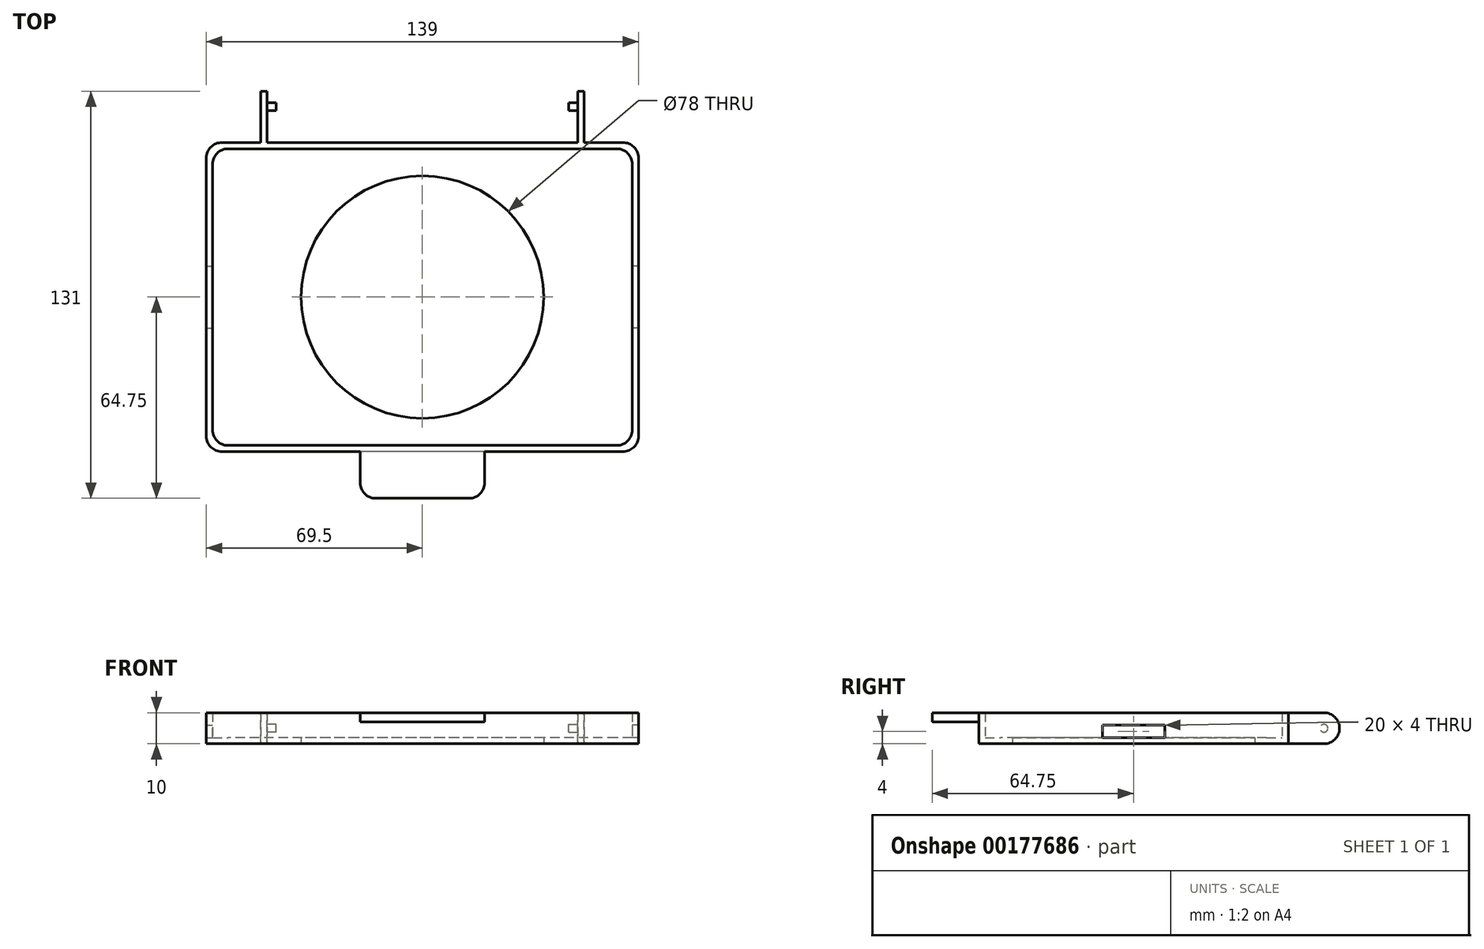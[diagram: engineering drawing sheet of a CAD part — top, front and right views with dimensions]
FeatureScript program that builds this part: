
annotation { "Feature Type Name" : "Feature", "Feature Type Description" : "" }
export const myFeature = defineFeature(function(context is Context, id is Id, definition is map)
    precondition{}
    {
        {
            var Q0;
            Q0=qCreatedBy(makeId("Top.planeOp"),FACE);
            var sketch = newSketch(context, id + "F0", { "sketchPlane" : qUnion([Q0])});
            skLineSegment(sketch, "E0.bottom", {"start": v(62.5, 47.75) * mm, "end": v(-62.5, 47.75) * mm});
            skLineSegment(sketch, "E0.top", {"start": v(62.5, -47.75) * mm, "end": v(-62.5, -47.75) * mm});
            skLineSegment(sketch, "E0.left", {"start": v(67.5, 42.75) * mm, "end": v(67.5, -42.75) * mm});
            skLineSegment(sketch, "E0.right", {"start": v(-67.5, 42.75) * mm, "end": v(-67.5, -42.75) * mm});
            skPoint(sketch, "E0.middle", {"position": v(0, 0) * mm});
            skLineSegment(sketch, "E1.0", {"start": v(64.5, 49.75) * mm, "end": v(-64.5, 49.75) * mm});
            skLineSegment(sketch, "E1.1", {"start": v(69.5, 44.75) * mm, "end": v(69.5, -44.75) * mm});
            skLineSegment(sketch, "E1.2", {"start": v(64.5, -49.75) * mm, "end": v(-64.5, -49.75) * mm});
            skLineSegment(sketch, "E1.3", {"start": v(-69.5, 44.75) * mm, "end": v(-69.5, -44.75) * mm});
            skPoint(sketch, "E2.visualSharp", {"position": v(-69.5, -49.75) * mm});
            skArc(sketch, "E2.filletArc", {"start": v(-69.5, -44.75) * mm, "mid": v(-68.04, -48.29) * mm, "end": v(-64.5, -49.75) * mm});
            skPoint(sketch, "E3.visualSharp", {"position": v(-69.5, 49.75) * mm});
            skArc(sketch, "E3.filletArc", {"start": v(-64.5, 49.75) * mm, "mid": v(-68.04, 48.29) * mm, "end": v(-69.5, 44.75) * mm});
            skPoint(sketch, "E4.visualSharp", {"position": v(69.5, -49.75) * mm});
            skArc(sketch, "E4.filletArc", {"start": v(64.5, -49.75) * mm, "mid": v(68.04, -48.29) * mm, "end": v(69.5, -44.75) * mm});
            skPoint(sketch, "E5.visualSharp", {"position": v(69.5, 49.75) * mm});
            skArc(sketch, "E5.filletArc", {"start": v(69.5, 44.75) * mm, "mid": v(68.04, 48.29) * mm, "end": v(64.5, 49.75) * mm});
            skPoint(sketch, "E6.visualSharp", {"position": v(67.5, 47.75) * mm});
            skArc(sketch, "E6.filletArc", {"start": v(67.5, 42.75) * mm, "mid": v(66.04, 46.29) * mm, "end": v(62.5, 47.75) * mm});
            skPoint(sketch, "E7.visualSharp", {"position": v(67.5, -47.75) * mm});
            skArc(sketch, "E7.filletArc", {"start": v(62.5, -47.75) * mm, "mid": v(66.04, -46.29) * mm, "end": v(67.5, -42.75) * mm});
            skPoint(sketch, "E8.visualSharp", {"position": v(-67.5, 47.75) * mm});
            skArc(sketch, "E8.filletArc", {"start": v(-62.5, 47.75) * mm, "mid": v(-66.04, 46.29) * mm, "end": v(-67.5, 42.75) * mm});
            skPoint(sketch, "E9.visualSharp", {"position": v(-67.5, -47.75) * mm});
            skArc(sketch, "E9.filletArc", {"start": v(-67.5, -42.75) * mm, "mid": v(-66.04, -46.29) * mm, "end": v(-62.5, -47.75) * mm});
            skCircle(sketch, "E10", {"center": v(0, 0) * mm, "radius": 39 * mm});
            skSolve(sketch);
        }
        {
            var Q0;
            Q0=makeQuery(id+"F0.imprint","IMPRINT",FACE,{"disambiguationData":[TD([[makeQuery(id+"F0.imprint","IMPRINT",EDGE,{"derivedFrom":sQuery(id+"F0.wireOp",EDGE,"E0.bottom")}),-1.0]])]});
            extrude(context, id + "F1", {"entities" : qUnion([Q0]), "depth" : 10 * mm});
        }
        {
            var Q0;
            Q0=makeQuery(id+"F0.imprint","IMPRINT",FACE,{"disambiguationData":[TD([[makeQuery(id+"F0.imprint","IMPRINT",EDGE,{"derivedFrom":sQuery(id+"F0.wireOp",EDGE,"E0.bottom")}),1.0]])]});
            extrude(context, id + "F2", {"entities" : qUnion([Q0]), "operationType" : NewBodyOperationType.ADD, "depth" : 2 * mm});
        }
        {
            var Q0;
            Q0=makeQuery(id+"F1.opExtrude","CAP_FACE",FACE,{"disambiguationData":[OSD([sQuery(id+"F0.wireOp",EDGE,"E0.bottom"),sQuery(id+"F0.wireOp",EDGE,"E0.top"),sQuery(id+"F0.wireOp",EDGE,"E0.left"),sQuery(id+"F0.wireOp",EDGE,"E0.right"),sQuery(id+"F0.wireOp",EDGE,"E1.0"),sQuery(id+"F0.wireOp",EDGE,"E1.1"),sQuery(id+"F0.wireOp",EDGE,"E1.2"),sQuery(id+"F0.wireOp",EDGE,"E1.3")])],"isStart":false});
            var sketch = newSketch(context, id + "F3", { "sketchPlane" : qUnion([Q0])});
            skLineSegment(sketch, "E11.bottom", {"start": v(-20, -49.75) * mm, "end": v(20, -49.75) * mm});
            skLineSegment(sketch, "E11.top", {"start": v(-15, -64.75) * mm, "end": v(15, -64.75) * mm});
            skLineSegment(sketch, "E11.left", {"start": v(-20, -49.75) * mm, "end": v(-20, -59.75) * mm});
            skLineSegment(sketch, "E11.right", {"start": v(20, -49.75) * mm, "end": v(20, -59.75) * mm});
            skPoint(sketch, "E12", {"position": v(0, -49.75) * mm});
            skPoint(sketch, "E13.visualSharp", {"position": v(-20, -64.75) * mm});
            skArc(sketch, "E13.filletArc", {"start": v(-20, -59.75) * mm, "mid": v(-18.54, -63.29) * mm, "end": v(-15, -64.75) * mm});
            skPoint(sketch, "E14.visualSharp", {"position": v(20, -64.75) * mm});
            skArc(sketch, "E14.filletArc", {"start": v(15, -64.75) * mm, "mid": v(18.54, -63.29) * mm, "end": v(20, -59.75) * mm});
            skSolve(sketch);
        }
        {
            var Q0;
            Q0=makeQuery(id+"F3.imprint","IMPRINT",FACE,{"disambiguationData":[TD([[makeQuery(id+"F3.imprint","IMPRINT",EDGE,{"derivedFrom":sQuery(id+"F3.wireOp",EDGE,"E11.bottom")}),1.0]])]});
            extrude(context, id + "F4", {"entities" : qUnion([Q0]), "operationType" : NewBodyOperationType.ADD, "oppositeDirection" : true, "depth" : 3 * mm});
        }
        {
            var Q0;
            Q0=makeQuery(id+"F1.opExtrude","SWEPT_FACE",FACE,{"disambiguationData":[OSD([sQuery(id+"F0.wireOp",EDGE,"E0.right")])]});
            var sketch = newSketch(context, id + "F5", { "sketchPlane" : qUnion([Q0])});
            skLineSegment(sketch, "E15.bottom", {"start": v(-10, 2) * mm, "end": v(10, 2) * mm});
            skLineSegment(sketch, "E15.top", {"start": v(-10, 6) * mm, "end": v(10, 6) * mm});
            skLineSegment(sketch, "E15.left", {"start": v(-10, 2) * mm, "end": v(-10, 6) * mm});
            skLineSegment(sketch, "E15.right", {"start": v(10, 2) * mm, "end": v(10, 6) * mm});
            skPoint(sketch, "E16", {"position": v(0, 2) * mm});
            skSolve(sketch);
        }
        {
            var Q0;
            Q0=makeQuery(id+"F5.imprint","IMPRINT",FACE,{"disambiguationData":[TD([[makeQuery(id+"F5.imprint","IMPRINT",EDGE,{"derivedFrom":sQuery(id+"F5.wireOp",EDGE,"E15.bottom")}),-1.0]])]});
            extrude(context, id + "F6", {"entities" : qUnion([Q0]), "operationType" : NewBodyOperationType.REMOVE, "endBound" : BoundingType.UP_TO_NEXT, "oppositeDirection" : true, "depth" : 25 * mm});
        }
        {
            var Q0;
            Q0=makeQuery(id+"F1.opExtrude","SWEPT_FACE",FACE,{"disambiguationData":[OSD([sQuery(id+"F0.wireOp",EDGE,"E0.left")])]});
            var sketch = newSketch(context, id + "F7", { "sketchPlane" : qUnion([Q0])});
            skLineSegment(sketch, "E17.0", {"start": v(10, 6) * mm, "end": v(10, 2) * mm});
            skLineSegment(sketch, "E18.0", {"start": v(10, 2) * mm, "end": v(-10, 2) * mm});
            skLineSegment(sketch, "E19.0", {"start": v(-10, 6) * mm, "end": v(10, 6) * mm});
            skLineSegment(sketch, "E20.0", {"start": v(-10, 6) * mm, "end": v(-10, 2) * mm});
            skSolve(sketch);
        }
        {
            var Q0;
            Q0=makeQuery(id+"F7.imprint","IMPRINT",FACE,{"disambiguationData":[TD([[makeQuery(id+"F7.imprint","IMPRINT",EDGE,{"derivedFrom":sQuery(id+"F7.wireOp",EDGE,"E17.0")}),-1.0]])]});
            extrude(context, id + "F8", {"entities" : qUnion([Q0]), "operationType" : NewBodyOperationType.REMOVE, "endBound" : BoundingType.UP_TO_NEXT, "oppositeDirection" : true, "depth" : 25 * mm});
        }
        {
            var Q0;
            Q0=makeQuery(id+"F1.opExtrude","SWEPT_FACE",FACE,{"disambiguationData":[OSD([sQuery(id+"F0.wireOp",EDGE,"E1.0")])]});
            var sketch = newSketch(context, id + "F9", { "sketchPlane" : qUnion([Q0])});
            skLineSegment(sketch, "E21.bottom", {"start": v(52, 0) * mm, "end": v(50, 0) * mm});
            skLineSegment(sketch, "E21.top", {"start": v(52, 10) * mm, "end": v(50, 10) * mm});
            skLineSegment(sketch, "E21.left", {"start": v(52, 0) * mm, "end": v(52, 10) * mm});
            skLineSegment(sketch, "E21.right", {"start": v(50, 0) * mm, "end": v(50, 10) * mm});
            skSolve(sketch);
        }
        {
            var Q0;
            Q0=makeQuery(id+"F9.imprint","IMPRINT",FACE,{"disambiguationData":[TD([[makeQuery(id+"F9.imprint","IMPRINT",EDGE,{"derivedFrom":sQuery(id+"F9.wireOp",EDGE,"E21.bottom")}),1.0]])]});
            var Q1;
            {var subQ0=sQuery(id+"F9.wireOp",EDGE,"c59233ef-eaf8-4a60-9904-21551acb0b020.MirrorCS");Q1=makeQuery(id+"F9.imprint","IMPRINT",FACE,{"disambiguationData":[TD([[makeQuery(id+"F9.imprint","IMPRINT",EDGE,{"derivedFrom":subQ0}),1.0]])]});}
            extrude(context, id + "F10", {"entities" : qUnion([Q0, Q1]), "operationType" : NewBodyOperationType.ADD, "depth" : 11.5 * mm});
        }
        {
            var Q0;
            Q0=makeQuery(id+"F10.opExtrude","SWEPT_FACE",FACE,{"disambiguationData":[OSD([sQuery(id+"F9.wireOp",EDGE,"E21.left")])]});
            var sketch = newSketch(context, id + "F11", { "sketchPlane" : qUnion([Q0])});
            skPoint(sketch, "E22", {"position": v(-61.25, 5) * mm});
            skCircle(sketch, "E23", {"center": v(-61.25, 5) * mm, "radius": 5 * mm});
            skSolve(sketch);
        }
        {
            var Q0;
            {var subQ1=sQuery(id+"F9.wireOp",EDGE,"E21.left");var subQ2=makeQuery(id+"F10.opExtrude","CAP_EDGE",EDGE,{"disambiguationData":[OSD([subQ1])],"isStart":false});Q0=makeQuery(id+"F11.imprint","IMPRINT",FACE,{"disambiguationData":[TD([[makeQuery(id+"F11.imprint","IMPRINT",EDGE,{"derivedFrom":subQ2}),1.0]])]});}
            extrude(context, id + "F12", {"entities" : qUnion([Q0]), "operationType" : NewBodyOperationType.ADD, "oppositeDirection" : true, "depth" : 2 * mm});
        }
        {
            var Q0;
            Q0=makeQuery(id+"F12.boolean.opBoolean","MERGE",FACE,{"derivedFrom":[makeQuery(id+"F10.opExtrude","SWEPT_FACE",FACE,{"disambiguationData":[OSD([sQuery(id+"F9.wireOp",EDGE,"E21.right")])]}),makeQuery(id+"F12.opExtrude","CAP_FACE",FACE,{"disambiguationData":[OSD([sQuery(id+"F9.wireOp",EDGE,"E21.left"),sQuery(id+"F11.wireOp",EDGE,"E23")])],"isStart":false})]});
            var sketch = newSketch(context, id + "F13", { "sketchPlane" : qUnion([Q0])});
            skCircle(sketch, "E24", {"center": v(61.25, 5) * mm, "radius": 1.25 * mm});
            skSolve(sketch);
        }
        {
            var Q0;
            Q0 = qSketchRegion(id + "F13", true);
            extrude(context, id + "F14", {"entities" : qUnion([Q0]), "operationType" : NewBodyOperationType.ADD, "depth" : 3 * mm});
        }
        {
            var Q0;
            Q0=qCreatedBy(makeId("Right.planeOp"),FACE);
            cPlane(context, id + "F15", {"entities" : qUnion([Q0]), "cplaneType" : CPlaneType.OFFSET, "offset" : 52 * mm, "width" : 150 * mm, "height" : 150 * mm});
        }
        {
            var Q0;
            Q0=qCreatedBy(id+"F15.planeOp",FACE);
            var sketch = newSketch(context, id + "F16", { "sketchPlane" : qUnion([Q0])});
            skLineSegment(sketch, "E25.0.0", {"start": v(49.75, 10) * mm, "end": v(49.75, 0) * mm});
            skLineSegment(sketch, "E25.0.1", {"start": v(49.75, 0) * mm, "end": v(61.25, 0) * mm});
            skArc(sketch, "E25.0.2", {"start": v(61.25, 0) * mm, "mid": v(66.25, 5) * mm, "end": v(61.25, 10) * mm});
            skLineSegment(sketch, "E25.0.3", {"start": v(61.25, 10) * mm, "end": v(49.75, 10) * mm});
            skCircle(sketch, "E26.0", {"center": v(61.25, 5) * mm, "radius": 1.25 * mm});
            skSolve(sketch);
        }
        {
            var Q0;
            Q0 = qSketchRegion(id + "F16", true);
            extrude(context, id + "F17", {"entities" : qUnion([Q0]), "operationType" : NewBodyOperationType.ADD, "oppositeDirection" : true, "depth" : 2 * mm});
        }
        {
            var Q0;
            Q0=makeQuery(id+"F16.imprint","IMPRINT",FACE,{"disambiguationData":[TD([[makeQuery(id+"F16.imprint","IMPRINT",EDGE,{"derivedFrom":sQuery(id+"F16.wireOp",EDGE,"E26.0")}),1.0]])]});
            extrude(context, id + "F18", {"entities" : qUnion([Q0]), "operationType" : NewBodyOperationType.ADD, "oppositeDirection" : true, "depth" : 5 * mm});
        }
    });
